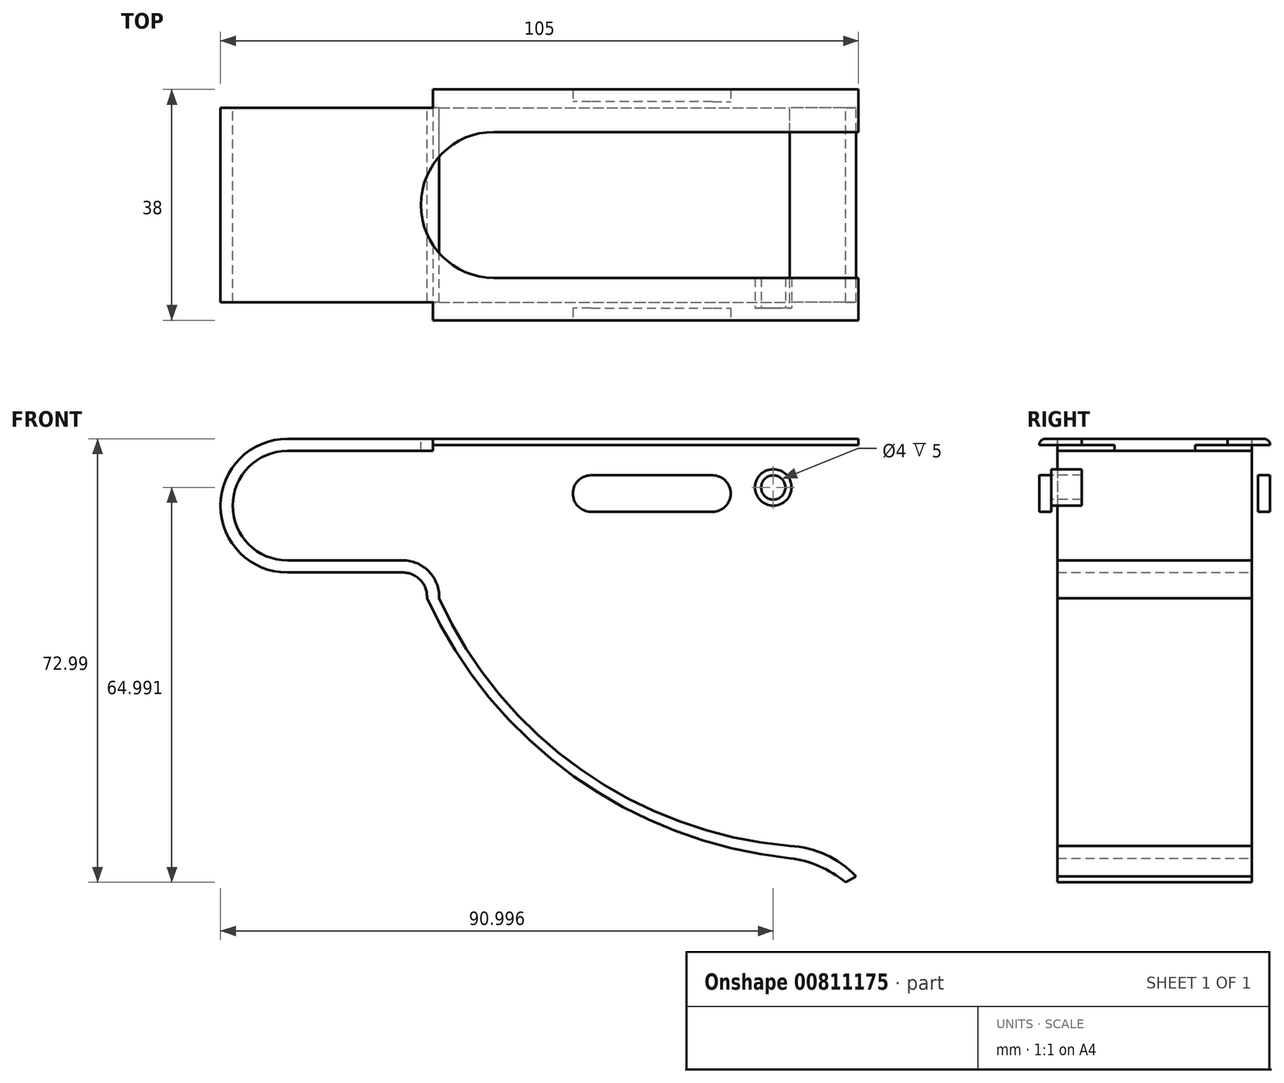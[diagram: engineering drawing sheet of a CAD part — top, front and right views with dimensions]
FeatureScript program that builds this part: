
annotation { "Feature Type Name" : "Feature", "Feature Type Description" : "" }
export const myFeature = defineFeature(function(context is Context, id is Id, definition is map)
    precondition{}
    {
        {
            var Q0;
            Q0=qCreatedBy(makeId("Front.planeOp"),FACE);
            var sketch = newSketch(context, id + "F0", { "sketchPlane" : qUnion([Q0])});
            skLineSegment(sketch, "E0.bottom", {"start": v(-47.71, 5.74) * mm, "end": v(46.29, 5.74) * mm});
            skLineSegment(sketch, "E0.top", {"start": v(-47.71, 3.74) * mm, "end": v(46.29, 3.74) * mm});
            skLineSegment(sketch, "E0.right", {"start": v(46.29, 5.74) * mm, "end": v(46.29, 3.74) * mm});
            skArc(sketch, "E1", {"start": v(-47.71, 3.74) * mm, "mid": v(-56.71, -5.26) * mm, "end": v(-47.71, -14.26) * mm});
            skLineSegment(sketch, "E2", {"start": v(-47.71, -14.26) * mm, "end": v(-28.71, -14.26) * mm});
            skArc(sketch, "E3", {"start": v(-22.72, -20.51) * mm, "mid": v(-24.38, -16.1) * mm, "end": v(-28.71, -14.26) * mm});
            skArc(sketch, "E4", {"start": v(-47.71, 5.74) * mm, "mid": v(-58.71, -5.26) * mm, "end": v(-47.71, -16.26) * mm});
            skLineSegment(sketch, "E5", {"start": v(-47.71, -16.26) * mm, "end": v(-28.71, -16.26) * mm});
            skArc(sketch, "E6", {"start": v(-24.72, -20.51) * mm, "mid": v(-25.8, -17.52) * mm, "end": v(-28.71, -16.26) * mm});
            skArc(sketch, "E7", {"start": v(-24.72, -20.51) * mm, "mid": v(-0.54, -49.82) * mm, "end": v(35, -63.26) * mm});
            skArc(sketch, "E8", {"start": v(-22.72, -20.51) * mm, "mid": v(0.62, -48.7) * mm, "end": v(35, -61.26) * mm});
            skArc(sketch, "E9", {"start": v(45.91, -66.26) * mm, "mid": v(40.94, -62.7) * mm, "end": v(35, -61.26) * mm});
            skArc(sketch, "E10", {"start": v(44.17, -67.25) * mm, "mid": v(39.87, -64.6) * mm, "end": v(35, -63.26) * mm});
            skLineSegment(sketch, "E11", {"start": v(44.17, -67.25) * mm, "end": v(45.91, -66.26) * mm});
            skSolve(sketch);
        }
        {
            var Q0;
            Q0=makeQuery(id+"F0.imprint","IMPRINT",FACE,{"disambiguationData":[TD([[makeQuery(id+"F0.imprint","IMPRINT",EDGE,{"derivedFrom":sQuery(id+"F0.wireOp",EDGE,"E0.bottom")}),-1.0]])]});
            extrude(context, id + "F1", {"entities" : qUnion([Q0]), "depth" : 16 * mm, "offsetDistance" : 25 * mm});
        }
        {
            var Q0;
            Q0=makeQuery(id+"F1.opExtrude","SWEPT_FACE",FACE,{"disambiguationData":[OSD([sQuery(id+"F0.wireOp",EDGE,"E0.bottom")])]});
            var sketch = newSketch(context, id + "F2", { "sketchPlane" : qUnion([Q0])});
            skLineSegment(sketch, "E12.bottom", {"start": v(46.29, -16) * mm, "end": v(-23.71, -16) * mm});
            skLineSegment(sketch, "E12.top", {"start": v(46.29, -19) * mm, "end": v(-23.71, -19) * mm});
            skLineSegment(sketch, "E12.left", {"start": v(46.29, -16) * mm, "end": v(46.29, -19) * mm});
            skLineSegment(sketch, "E12.right", {"start": v(-23.71, -16) * mm, "end": v(-23.71, -19) * mm});
            skSolve(sketch);
        }
        {
            var Q0;
            Q0=makeQuery(id+"F2.imprint","IMPRINT",FACE,{"disambiguationData":[TD([[makeQuery(id+"F2.imprint","IMPRINT",EDGE,{"derivedFrom":sQuery(id+"F2.wireOp",EDGE,"E12.bottom")}),-1.0]])]});
            extrude(context, id + "F3", {"entities" : qUnion([Q0]), "operationType" : NewBodyOperationType.ADD, "oppositeDirection" : true, "depth" : 2 * mm, "offsetDistance" : 25 * mm});
        }
        {
            var Q0;
            Q0=makeQuery(id+"F3.opExtrude","SWEPT_FACE",FACE,{"disambiguationData":[OSD([sQuery(id+"F2.wireOp",EDGE,"E12.top")])]});
            var sketch = newSketch(context, id + "F4", { "sketchPlane" : qUnion([Q0])});
            skLineSegment(sketch, "E13.bottom", {"start": v(46.29, 5.74) * mm, "end": v(-3.71, 5.74) * mm});
            skLineSegment(sketch, "E13.top", {"start": v(46.29, -8.26) * mm, "end": v(-3.71, -8.26) * mm});
            skLineSegment(sketch, "E13.left", {"start": v(46.29, 5.74) * mm, "end": v(46.29, -8.26) * mm});
            skLineSegment(sketch, "E13.right", {"start": v(-3.71, 5.74) * mm, "end": v(-3.71, -8.26) * mm});
            skSolve(sketch);
        }
        {
            var Q0;
            {var subQ0=sQuery(id+"F4.wireOp",EDGE,"E13.top");Q0=makeQuery(id+"F4.imprint","IMPRINT",FACE,{"disambiguationData":[TD([[makeQuery(id+"F4.imprint","IMPRINT",EDGE,{"derivedFrom":subQ0}),-1.0]])]});}
            extrude(context, id + "F5", {"entities" : qUnion([Q0]), "operationType" : NewBodyOperationType.ADD, "oppositeDirection" : true, "depth" : 2 * mm, "offsetDistance" : 25 * mm});
        }
        {
            var Q0;
            Q0=makeQuery(id+"F3.opExtrude","CAP_EDGE",EDGE,{"disambiguationData":[OSD([sQuery(id+"F2.wireOp",EDGE,"E12.top")])],"isStart":true});
            var Q1;
            Q1=makeQuery(id+"F5.opExtrude","CAP_EDGE",EDGE,{"disambiguationData":[OSD([sQuery(id+"F2.wireOp",EDGE,"E12.top")])],"isStart":false});
            fillet(context, id + "F6", {"entities" : qUnion([Q0, Q1]), "radius" : 1 * mm, "tangentPropagation" : true, "allowEdgeOverflow" : false});
        }
        {
            var Q0;
            Q0=makeQuery(id+"F1.opExtrude","SWEPT_BODY",BODY,{"disambiguationData":[OSD([sQuery(id+"F0.wireOp",EDGE,"E0.bottom"),sQuery(id+"F0.wireOp",EDGE,"E0.top"),sQuery(id+"F0.wireOp",EDGE,"E0.right"),sQuery(id+"F0.wireOp",EDGE,"E1"),sQuery(id+"F0.wireOp",EDGE,"E2"),sQuery(id+"F0.wireOp",EDGE,"E3"),sQuery(id+"F0.wireOp",EDGE,"E4"),sQuery(id+"F0.wireOp",EDGE,"E5"),sQuery(id+"F0.wireOp",EDGE,"E6"),sQuery(id+"F0.wireOp",EDGE,"E7"),sQuery(id+"F0.wireOp",EDGE,"E8"),sQuery(id+"F0.wireOp",EDGE,"E9"),sQuery(id+"F0.wireOp",EDGE,"E10"),sQuery(id+"F0.wireOp",EDGE,"E11")])]});
            var Q1;
            Q1=qCreatedBy(makeId("Front.planeOp"),FACE);
            mirror(context, id + "F7", {"operationType" : NewBodyOperationType.ADD, "entities" : qUnion([Q0]), "mirrorPlane" : qUnion([Q1])});
        }
        {
            var Q0;
            {var subQ0=makeQuery(id+"F3.boolean.opBoolean","MERGE",FACE,{"derivedFrom":[makeQuery(id+"F1.opExtrude","SWEPT_FACE",FACE,{"disambiguationData":[OSD([sQuery(id+"F0.wireOp",EDGE,"E0.bottom")])]}),makeQuery(id+"F3.opExtrude","CAP_FACE",FACE,{"disambiguationData":[OSD([sQuery(id+"F2.wireOp",EDGE,"E12.bottom"),sQuery(id+"F2.wireOp",EDGE,"E12.top"),sQuery(id+"F2.wireOp",EDGE,"E12.left"),sQuery(id+"F2.wireOp",EDGE,"E12.right")])],"isStart":true})]});Q0=makeQuery(id+"F7.boolean.opBoolean","MERGE",FACE,{"derivedFrom":[subQ0,makeQuery(id+"F7.opPattern","COPY",FACE,{"derivedFrom":subQ0,"instanceName":"1"})]});}
            var sketch = newSketch(context, id + "F8", { "sketchPlane" : qUnion([Q0])});
            skArc(sketch, "E14", {"start": v(-13.71, 12) * mm, "mid": v(-25.71, 0) * mm, "end": v(-13.71, -12) * mm});
            skLineSegment(sketch, "E15", {"start": v(-13.71, -12) * mm, "end": v(46.29, -12) * mm});
            skLineSegment(sketch, "E16", {"start": v(-13.71, 12) * mm, "end": v(46.29, 12) * mm});
            skLineSegment(sketch, "E17", {"start": v(46.29, 12) * mm, "end": v(46.29, -12) * mm});
            skSolve(sketch);
        }
        {
            var Q0;
            Q0=makeQuery(id+"F8.imprint","IMPRINT",FACE,{"disambiguationData":[TD([[makeQuery(id+"F8.imprint","IMPRINT",EDGE,{"derivedFrom":sQuery(id+"F8.wireOp",EDGE,"E14")}),1.0]])]});
            extrude(context, id + "F9", {"entities" : qUnion([Q0]), "operationType" : NewBodyOperationType.REMOVE, "oppositeDirection" : true, "depth" : 2 * mm, "offsetDistance" : 25 * mm});
        }
        {
            var Q0;
            {var subQ0=sQuery(id+"F2.wireOp",EDGE,"E12.top");Q0=makeQuery(id+"F5.boolean.opBoolean","MERGE",FACE,{"derivedFrom":[makeQuery(id+"F3.opExtrude","SWEPT_FACE",FACE,{"disambiguationData":[OSD([subQ0])]}),makeQuery(id+"F5.opExtrude","CAP_FACE",FACE,{"disambiguationData":[OSD([subQ0,sQuery(id+"F4.wireOp",EDGE,"E13.top"),sQuery(id+"F4.wireOp",EDGE,"E13.left"),sQuery(id+"F4.wireOp",EDGE,"E13.right")])],"isStart":true})]});}
            var sketch = newSketch(context, id + "F10", { "sketchPlane" : qUnion([Q0])});
            skLineSegment(sketch, "E18", {"start": v(2.29, -3.26) * mm, "end": v(22.29, -3.26) * mm});
            skArc(sketch, "E19.0.startCap", {"start": v(2.29, -6.26) * mm, "mid": v(-0.71, -3.26) * mm, "end": v(2.29, -0.26) * mm});
            skArc(sketch, "E19.0.endCap", {"start": v(22.29, -0.26) * mm, "mid": v(25.29, -3.26) * mm, "end": v(22.29, -6.26) * mm});
            skLineSegment(sketch, "E19.0.left", {"start": v(2.29, -0.26) * mm, "end": v(22.29, -0.26) * mm});
            skLineSegment(sketch, "E19.0.right", {"start": v(2.29, -6.26) * mm, "end": v(22.29, -6.26) * mm});
            skSolve(sketch);
        }
        {
            var Q0;
            Q0=makeQuery(id+"F10.imprint","IMPRINT",FACE,{"disambiguationData":[TD([[makeQuery(id+"F10.imprint","IMPRINT",EDGE,{"derivedFrom":sQuery(id+"F10.wireOp",EDGE,"E19.0.startCap")}),-1.0]])]});
            extrude(context, id + "F11", {"entities" : qUnion([Q0]), "operationType" : NewBodyOperationType.REMOVE, "endBound" : BoundingType.THROUGH_ALL, "oppositeDirection" : true, "depth" : 25 * mm, "offsetDistance" : 25 * mm});
        }
        {
            var Q0;
            {var subQ0=sQuery(id+"F2.wireOp",EDGE,"E12.top");Q0=makeQuery(id+"F5.boolean.opBoolean","MERGE",FACE,{"derivedFrom":[makeQuery(id+"F3.opExtrude","SWEPT_FACE",FACE,{"disambiguationData":[OSD([subQ0])]}),makeQuery(id+"F5.opExtrude","CAP_FACE",FACE,{"disambiguationData":[OSD([subQ0,sQuery(id+"F4.wireOp",EDGE,"E13.top"),sQuery(id+"F4.wireOp",EDGE,"E13.left"),sQuery(id+"F4.wireOp",EDGE,"E13.right")])],"isStart":true})]});}
            var sketch = newSketch(context, id + "F12", { "sketchPlane" : qUnion([Q0])});
            skPoint(sketch, "E20", {"position": v(32.29, -2.26) * mm});
            skSolve(sketch);
        }
        {
            var Q0;
            Q0=sQuery(id+"F12.wireOp",VERTEX,"E20");
            var Q1;
            Q1=makeQuery(id+"F1.opExtrude","SWEPT_BODY",BODY,{"disambiguationData":[OSD([sQuery(id+"F0.wireOp",EDGE,"E0.bottom"),sQuery(id+"F0.wireOp",EDGE,"E0.top"),sQuery(id+"F0.wireOp",EDGE,"E0.right"),sQuery(id+"F0.wireOp",EDGE,"E1"),sQuery(id+"F0.wireOp",EDGE,"E2"),sQuery(id+"F0.wireOp",EDGE,"E3"),sQuery(id+"F0.wireOp",EDGE,"E4"),sQuery(id+"F0.wireOp",EDGE,"E5"),sQuery(id+"F0.wireOp",EDGE,"E6"),sQuery(id+"F0.wireOp",EDGE,"E7"),sQuery(id+"F0.wireOp",EDGE,"E8"),sQuery(id+"F0.wireOp",EDGE,"E9"),sQuery(id+"F0.wireOp",EDGE,"E10"),sQuery(id+"F0.wireOp",EDGE,"E11")])]});
            hole(context, id + "F13", {"style" : HoleStyle.SIMPLE, "endStyle" : HoleEndStyle.THROUGH, "holeDiameter" : 4 * mm, "majorDiameter" : 5 * mm, "isTappedThrough" : true, "tappedDepth" : 12 * mm, "tapClearance" : 3, "locations" : qUnion([Q0]), "scope" : qUnion([Q1])});
        }
        {
            var Q0;
            Q0=makeQuery(id+"F5.opExtrude","CAP_FACE",FACE,{"disambiguationData":[OSD([sQuery(id+"F2.wireOp",EDGE,"E12.top"),sQuery(id+"F4.wireOp",EDGE,"E13.top"),sQuery(id+"F4.wireOp",EDGE,"E13.left"),sQuery(id+"F4.wireOp",EDGE,"E13.right")])],"isStart":false});
            var sketch = newSketch(context, id + "F14", { "sketchPlane" : qUnion([Q0])});
            skCircle(sketch, "E21.0", {"center": v(-32.29, -2.26) * mm, "radius": 2 * mm});
            skCircle(sketch, "E22.0", {"center": v(-32.29, -2.26) * mm, "radius": 3 * mm});
            skSolve(sketch);
        }
        {
            var Q0;
            Q0=makeQuery(id+"F14.imprint","IMPRINT",FACE,{"disambiguationData":[TD([[makeQuery(id+"F14.imprint","IMPRINT",EDGE,{"derivedFrom":sQuery(id+"F14.wireOp",EDGE,"E21.0")}),-1.0]])]});
            extrude(context, id + "F15", {"entities" : qUnion([Q0]), "operationType" : NewBodyOperationType.ADD, "depth" : 5 * mm, "offsetDistance" : 25 * mm});
        }
        {
            var Q0;
            Q0=qCreatedBy(makeId("Right.planeOp"),FACE);
            cPlane(context, id + "F16", {"entities" : qUnion([Q0]), "cplaneType" : CPlaneType.OFFSET, "offset" : 32.2 * mm, "width" : 150 * mm, "height" : 150 * mm});
        }
    });
